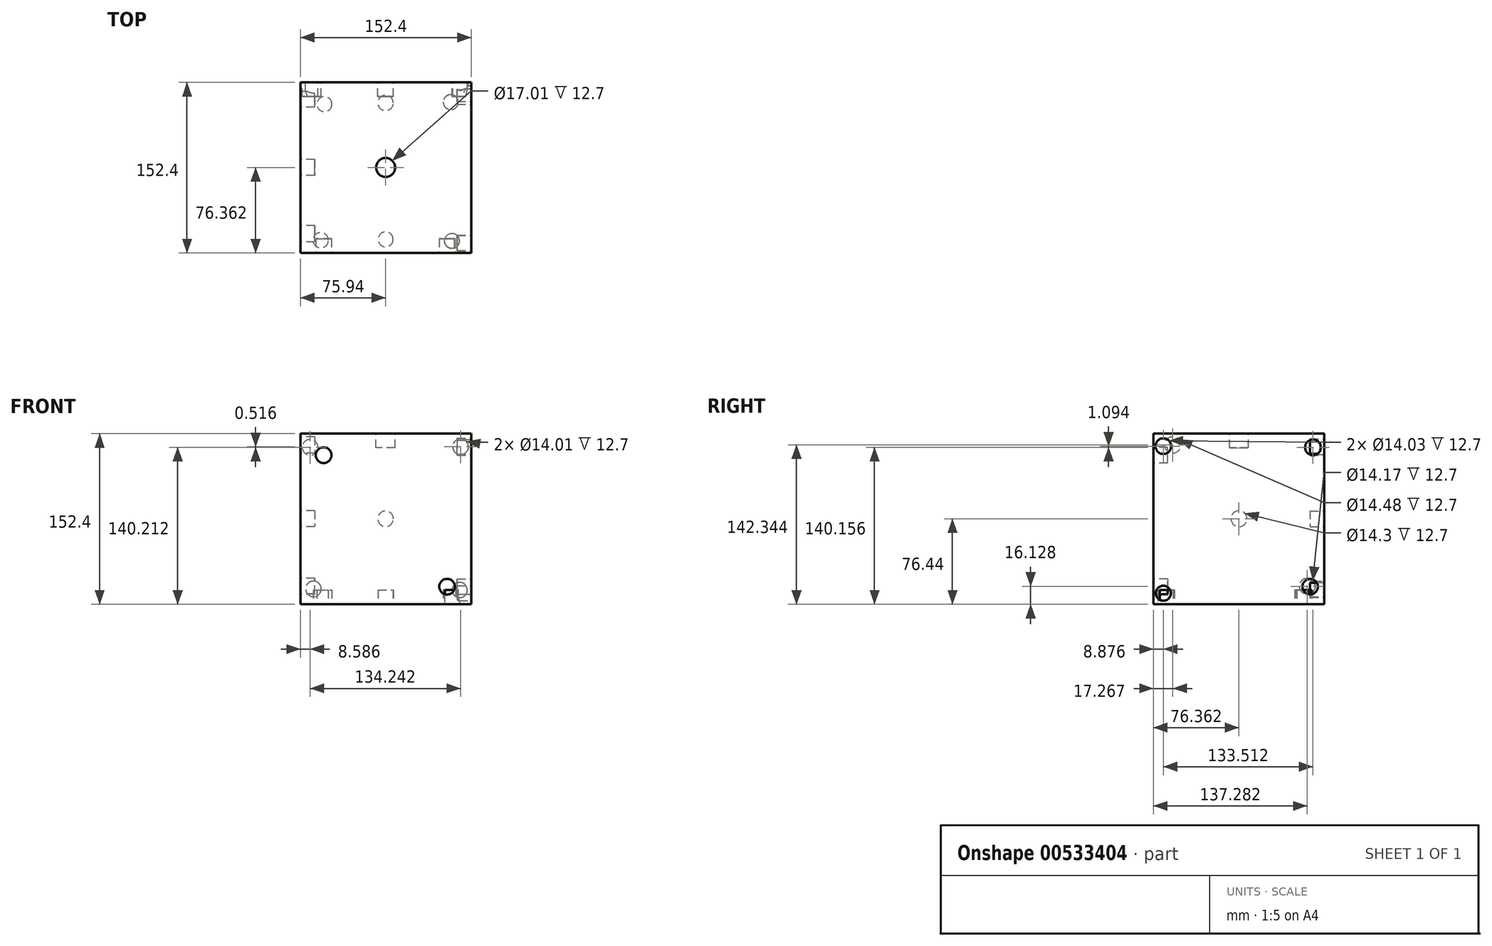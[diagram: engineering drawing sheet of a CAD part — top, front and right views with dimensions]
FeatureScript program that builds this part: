
annotation { "Feature Type Name" : "Feature", "Feature Type Description" : "" }
export const myFeature = defineFeature(function(context is Context, id is Id, definition is map)
    precondition{}
    {
        {
            var Q0;
            Q0=qCreatedBy(makeId("Front.planeOp"),FACE);
            var sketch = newSketch(context, id + "F0", { "sketchPlane" : qUnion([Q0])});
            skLineSegment(sketch, "E0", {"start": v(-75.94, 75.96) * mm, "end": v(76.46, 75.96) * mm});
            skLineSegment(sketch, "E1", {"start": v(-75.94, 75.96) * mm, "end": v(-75.94, -76.44) * mm});
            skLineSegment(sketch, "E2", {"start": v(-75.94, -76.44) * mm, "end": v(76.46, -76.44) * mm});
            skLineSegment(sketch, "E3", {"start": v(76.46, 75.96) * mm, "end": v(76.46, -76.44) * mm});
            skSolve(sketch);
        }
        {
            var Q0;
            Q0=makeQuery(id+"F0.imprint","IMPRINT",FACE,{"disambiguationData":[TD([[makeQuery(id+"F0.imprint","IMPRINT",EDGE,{"derivedFrom":sQuery(id+"F0.wireOp",EDGE,"E0")}),-1.0]])]});
            extrude(context, id + "F1", {"entities" : qUnion([Q0]), "depth" : 152.4 * mm, "offsetDistance" : 25.4 * mm});
        }
        {
            var Q0;
            Q0=makeQuery(id+"F1.opExtrude","SWEPT_FACE",FACE,{"disambiguationData":[OSD([sQuery(id+"F0.wireOp",EDGE,"E0")])]});
            var sketch = newSketch(context, id + "F2", { "sketchPlane" : qUnion([Q0])});
            skCircle(sketch, "E4", {"center": v(0, -76.04) * mm, "radius": 8.5 * mm});
            skSolve(sketch);
        }
        {
            var Q0;
            Q0 = qSketchRegion(id + "F2", true);
            extrude(context, id + "F3", {"entities" : qUnion([Q0]), "operationType" : NewBodyOperationType.REMOVE, "oppositeDirection" : true, "depth" : 12.7 * mm, "offsetDistance" : 25.4 * mm});
        }
        {
            var Q0;
            Q0=makeQuery(id+"F1.opExtrude","CAP_FACE",FACE,{"disambiguationData":[OSD([sQuery(id+"F0.wireOp",EDGE,"E0"),sQuery(id+"F0.wireOp",EDGE,"E1"),sQuery(id+"F0.wireOp",EDGE,"E2"),sQuery(id+"F0.wireOp",EDGE,"E3")])],"isStart":true});
            var sketch = newSketch(context, id + "F4", { "sketchPlane" : qUnion([Q0])});
            skCircle(sketch, "E5", {"center": v(64.44, -62.62) * mm, "radius": 6.95 * mm});
            skCircle(sketch, "E6", {"center": v(-66.16, -63.65) * mm, "radius": 6.77 * mm});
            skCircle(sketch, "E7", {"center": v(-66.89, 65.84) * mm, "radius": 6.75 * mm});
            skCircle(sketch, "E8", {"center": v(67.35, 63.77) * mm, "radius": 7 * mm});
            skSolve(sketch);
        }
        {
            var Q0;
            Q0=makeQuery(id+"F4.imprint","IMPRINT",FACE,{"disambiguationData":[TD([[makeQuery(id+"F4.imprint","IMPRINT",EDGE,{"derivedFrom":sQuery(id+"F4.wireOp",EDGE,"E8")}),1.0]])]});
            var Q1;
            Q1=makeQuery(id+"F4.imprint","IMPRINT",FACE,{"disambiguationData":[TD([[makeQuery(id+"F4.imprint","IMPRINT",EDGE,{"derivedFrom":sQuery(id+"F4.wireOp",EDGE,"E5")}),1.0]])]});
            var Q2;
            Q2=makeQuery(id+"F4.imprint","IMPRINT",FACE,{"disambiguationData":[TD([[makeQuery(id+"F4.imprint","IMPRINT",EDGE,{"derivedFrom":sQuery(id+"F4.wireOp",EDGE,"E6")}),1.0]])]});
            var Q3;
            Q3=sQuery(id+"F4.wireOp",EDGE,"E7");
            extrude(context, id + "F5", {"entities" : qUnion([Q0, Q1, Q2]), "operationType" : NewBodyOperationType.REMOVE, "surfaceEntities" : qUnion([Q3]), "oppositeDirection" : true, "depth" : 12.7 * mm, "offsetDistance" : 25.4 * mm});
        }
        {
            var Q0;
            Q0=makeQuery(id+"F1.opExtrude","CAP_FACE",FACE,{"disambiguationData":[OSD([sQuery(id+"F0.wireOp",EDGE,"E0"),sQuery(id+"F0.wireOp",EDGE,"E1"),sQuery(id+"F0.wireOp",EDGE,"E2"),sQuery(id+"F0.wireOp",EDGE,"E3")])],"isStart":true});
            var sketch = newSketch(context, id + "F6", { "sketchPlane" : qUnion([Q0])});
            skCircle(sketch, "E9", {"center": v(-66.89, 64.29) * mm, "radius": 7 * mm});
            skCircle(sketch, "E10", {"center": v(0, 0) * mm, "radius": 6.95 * mm});
            skSolve(sketch);
        }
        {
            var Q0;
            Q0 = qSketchRegion(id + "F6", true);
            extrude(context, id + "F7", {"entities" : qUnion([Q0]), "operationType" : NewBodyOperationType.REMOVE, "oppositeDirection" : true, "depth" : 12.7 * mm, "offsetDistance" : 25.4 * mm});
        }
        {
            var Q0;
            Q0=makeQuery(id+"F1.opExtrude","CAP_FACE",FACE,{"disambiguationData":[OSD([sQuery(id+"F0.wireOp",EDGE,"E0"),sQuery(id+"F0.wireOp",EDGE,"E1"),sQuery(id+"F0.wireOp",EDGE,"E2"),sQuery(id+"F0.wireOp",EDGE,"E3")])],"isStart":false});
            var sketch = newSketch(context, id + "F8", { "sketchPlane" : qUnion([Q0])});
            skCircle(sketch, "E11", {"center": v(-55.32, 56.78) * mm, "radius": 7.05 * mm});
            skCircle(sketch, "E12", {"center": v(54.85, -60.68) * mm, "radius": 7.02 * mm});
            skSolve(sketch);
        }
        {
            var Q0;
            Q0 = qSketchRegion(id + "F8", true);
            extrude(context, id + "F9", {"entities" : qUnion([Q0]), "operationType" : NewBodyOperationType.REMOVE, "oppositeDirection" : true, "depth" : 12.7 * mm, "offsetDistance" : 25.4 * mm});
        }
        {
            var Q0;
            Q0=makeQuery(id+"F1.opExtrude","SWEPT_FACE",FACE,{"disambiguationData":[OSD([sQuery(id+"F0.wireOp",EDGE,"E1")])]});
            var sketch = newSketch(context, id + "F10", { "sketchPlane" : qUnion([Q0])});
            skCircle(sketch, "E13", {"center": v(15.12, -60.31) * mm, "radius": 7.08 * mm});
            skCircle(sketch, "E14", {"center": v(76.04, 0) * mm, "radius": 7.15 * mm});
            skCircle(sketch, "E15", {"center": v(135.13, 65.9) * mm, "radius": 7.24 * mm});
            skSolve(sketch);
        }
        {
            var Q0;
            Q0 = qSketchRegion(id + "F10", true);
            extrude(context, id + "F11", {"entities" : qUnion([Q0]), "operationType" : NewBodyOperationType.REMOVE, "oppositeDirection" : true, "depth" : 12.7 * mm, "offsetDistance" : 25.4 * mm});
        }
        {
            var Q0;
            Q0=makeQuery(id+"F1.opExtrude","SWEPT_FACE",FACE,{"disambiguationData":[OSD([sQuery(id+"F0.wireOp",EDGE,"E2")])]});
            var sketch = newSketch(context, id + "F12", { "sketchPlane" : qUnion([Q0])});
            skCircle(sketch, "E16", {"center": v(58.13, 17.67) * mm, "radius": 6.7 * mm});
            skCircle(sketch, "E17", {"center": v(0, 18.4) * mm, "radius": 6.88 * mm});
            skCircle(sketch, "E18", {"center": v(-54.59, 19.5) * mm, "radius": 6.7 * mm});
            skCircle(sketch, "E19", {"center": v(0, 140.24) * mm, "radius": 6.69 * mm});
            skCircle(sketch, "E20", {"center": v(-57.87, 140.97) * mm, "radius": 6.81 * mm});
            skCircle(sketch, "E21", {"center": v(59.23, 141.7) * mm, "radius": 6.66 * mm});
            skSolve(sketch);
        }
        {
            var Q0;
            Q0 = qSketchRegion(id + "F12", true);
            extrude(context, id + "F13", {"entities" : qUnion([Q0]), "operationType" : NewBodyOperationType.REMOVE, "oppositeDirection" : true, "depth" : 12.7 * mm, "offsetDistance" : 25.4 * mm});
        }
        {
            var Q0;
            Q0=makeQuery(id+"F1.opExtrude","SWEPT_FACE",FACE,{"disambiguationData":[OSD([sQuery(id+"F0.wireOp",EDGE,"E3")])]});
            var sketch = newSketch(context, id + "F14", { "sketchPlane" : qUnion([Q0])});
            skCircle(sketch, "E22", {"center": v(-10.01, 63.72) * mm, "radius": 7.02 * mm});
            skCircle(sketch, "E23", {"center": v(-12.56, -60.68) * mm, "radius": 6.88 * mm});
            skCircle(sketch, "E24", {"center": v(-143.52, 64.8) * mm, "radius": 7.02 * mm});
            skCircle(sketch, "E25", {"center": v(-143.52, -66.51) * mm, "radius": 6.73 * mm});
            skSolve(sketch);
        }
        {
            var Q0;
            Q0 = qSketchRegion(id + "F14", true);
            extrude(context, id + "F15", {"entities" : qUnion([Q0]), "operationType" : NewBodyOperationType.REMOVE, "oppositeDirection" : true, "depth" : 12.7 * mm, "offsetDistance" : 25.4 * mm});
        }
    });
